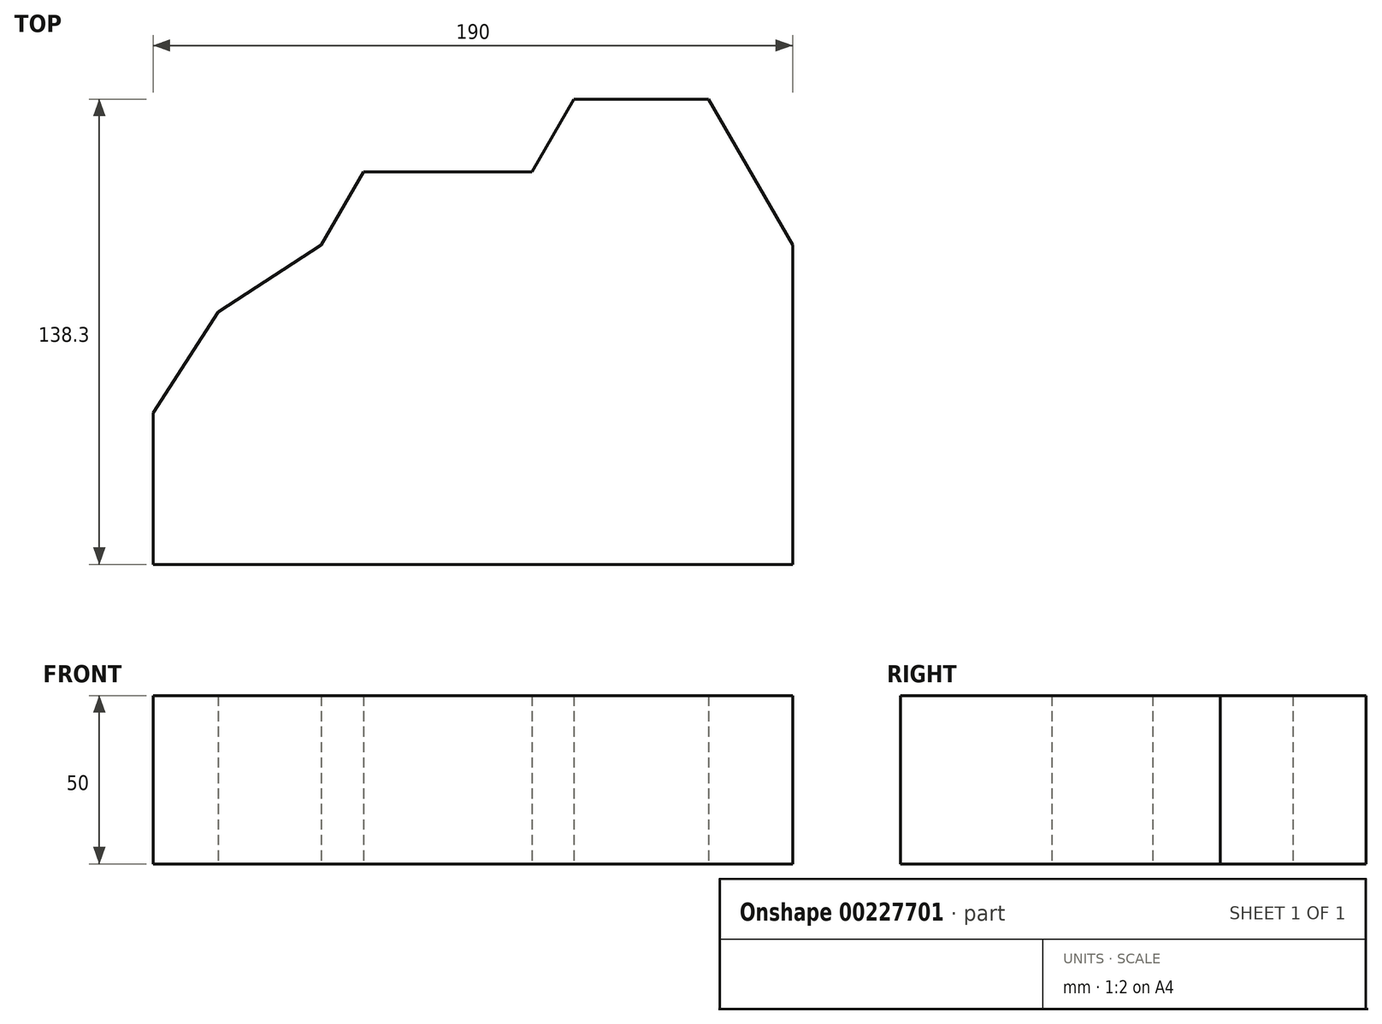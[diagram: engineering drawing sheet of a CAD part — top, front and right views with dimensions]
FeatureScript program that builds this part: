
annotation { "Feature Type Name" : "Feature", "Feature Type Description" : "" }
export const myFeature = defineFeature(function(context is Context, id is Id, definition is map)
    precondition{}
    {
        {
            var Q0;
            Q0=qCreatedBy(makeId("Top.planeOp"),FACE);
            var sketch = newSketch(context, id + "F0", { "sketchPlane" : qUnion([Q0])});
            skLineSegment(sketch, "E0", {"start": v(-62.5, -95) * mm, "end": v(127.5, -95) * mm});
            skLineSegment(sketch, "E1", {"start": v(127.5, -95) * mm, "end": v(127.5, 0) * mm});
            skLineSegment(sketch, "E2", {"start": v(127.5, 0) * mm, "end": v(102.5, 43.3) * mm});
            skLineSegment(sketch, "E3", {"start": v(102.5, 43.3) * mm, "end": v(62.5, 43.3) * mm});
            skLineSegment(sketch, "E4", {"start": v(62.5, 43.3) * mm, "end": v(50, 21.65) * mm});
            skLineSegment(sketch, "E5", {"start": v(50, 21.65) * mm, "end": v(0, 21.65) * mm});
            skLineSegment(sketch, "E6", {"start": v(0, 21.65) * mm, "end": v(-12.5, 0) * mm});
            skLineSegment(sketch, "E7", {"start": v(-12.5, 0) * mm, "end": v(-43.12, -20) * mm});
            skLineSegment(sketch, "E8", {"start": v(-43.12, -20) * mm, "end": v(-62.5, -50) * mm});
            skLineSegment(sketch, "E9", {"start": v(-62.5, -95) * mm, "end": v(-62.5, -50) * mm});
            skLineSegment(sketch, "E10", {"start": v(127.5, 0) * mm, "end": v(127.5, 69.82) * mm, "construction": true});
            skLineSegment(sketch, "E11", {"start": v(50, 21.65) * mm, "end": v(50, 52.36) * mm, "construction": true});
            skLineSegment(sketch, "E12", {"start": v(-12.5, 0) * mm, "end": v(-12.5, 27.54) * mm, "construction": true});
            skSolve(sketch);
        }
        {
            var Q0;
            Q0 = qSketchRegion(id + "F0", true);
            extrude(context, id + "F1", {"entities" : qUnion([Q0]), "depth" : 50 * mm});
        }
    });
